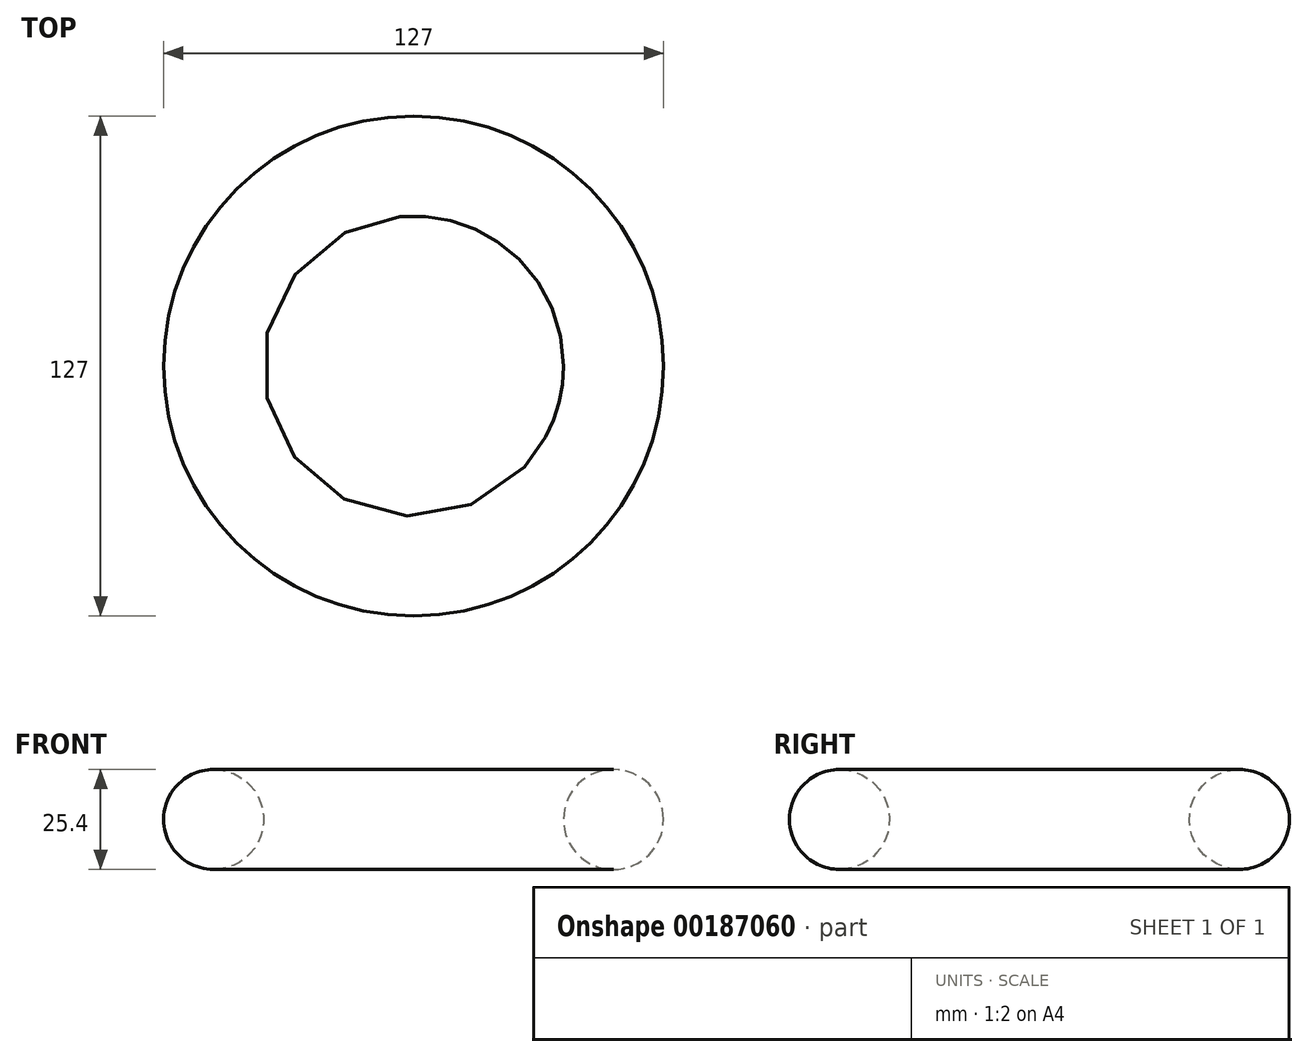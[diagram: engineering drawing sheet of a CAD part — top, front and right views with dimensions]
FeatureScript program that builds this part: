
annotation { "Feature Type Name" : "Feature", "Feature Type Description" : "" }
export const myFeature = defineFeature(function(context is Context, id is Id, definition is map)
    precondition{}
    {
        {
            var Q0;
            Q0=qCreatedBy(makeId("Front.planeOp"),FACE);
            var sketch = newSketch(context, id + "F0", { "sketchPlane" : qUnion([Q0])});
            skCircle(sketch, "E0", {"center": v(50.8, 0) * mm, "radius": 12.7 * mm});
            skLineSegment(sketch, "E1", {"start": v(0, 21.82) * mm, "end": v(0, 0) * mm});
            skSolve(sketch);
        }
        {
            var Q0;
            Q0=makeQuery(id+"F0.imprint","IMPRINT",FACE,{"disambiguationData":[TD([[makeQuery(id+"F0.imprint","IMPRINT",EDGE,{"derivedFrom":sQuery(id+"F0.wireOp",EDGE,"E0")}),1.0]])]});
            var Q1;
            Q1=sQuery(id+"F0.wireOp",EDGE,"E1");
            revolve(context, id + "F1", {"entities" : qUnion([Q0]), "axis" : qUnion([Q1]), "revolveType" : RevolveType.FULL});
        }
    });
